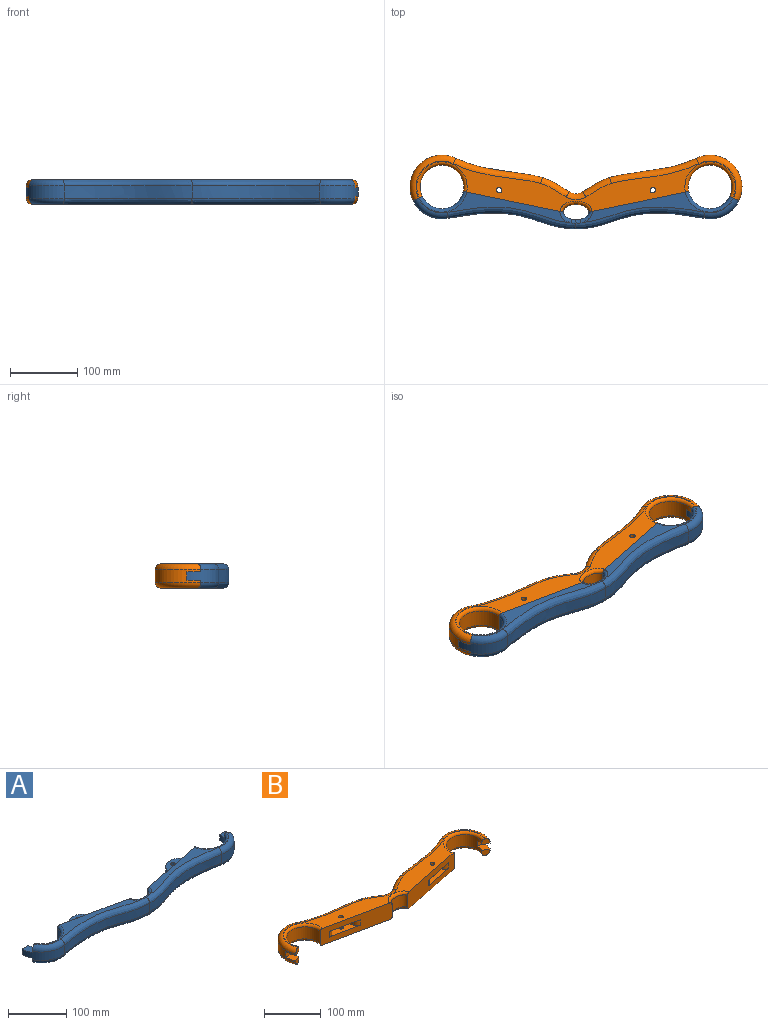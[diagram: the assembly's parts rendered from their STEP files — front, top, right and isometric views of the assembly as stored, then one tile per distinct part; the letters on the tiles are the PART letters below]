
ASSEMBLY  parts=2 mates=1
PART A: 55 faces, bbox 509.2x69.1x37.5 mm
  f0: plane 227x45.55mm, normal (0,0,1), area 2219.1mm2, adj f18,f32,f39,f40,f48,f52
  f1: plane 227x45.55mm, normal (0,0,-1), area 2219.3mm2, adj f20,f27,f33,f34,f45,f46
  f2: cylinder r=47.5mm len=56.8mm, axis (0,0,-1), area 1384.6mm2, adj f3,f17,f25,f26,f31,f32,f36,f40
  f3: plane 15x12mm, normal (0,1,0), area 180mm2, adj f2,f4,f26,f31
  f4: cylinder r=32.5mm len=64.32mm, axis (0,0,-1), area 2279.5mm2, adj f3,f18,f25,f26,f31,f32,f41,f52
  f5: cylinder r=10mm len=12mm, axis (0,0,-1), area 148.4mm2, adj f6,f18,f23,f24
  f6: cylinder r=24.42mm len=45.19mm, axis (0,0,-1), area 725.1mm2, adj f5,f7,f23,f24
  f7: cylinder r=10mm len=12mm, axis (0,0,-1), area 148.4mm2, adj f6,f18,f23,f24
  f8: cylinder r=10mm len=12mm, axis (0,0,-1), area 148.4mm2, adj f9,f20,f21,f22
  f9: cylinder r=24.42mm len=45.19mm, axis (0,0,-1), area 725.1mm2, adj f8,f10,f21,f22
  f10: cylinder r=10mm len=12mm, axis (0,0,-1), area 148.4mm2, adj f9,f20,f21,f22
  f11: cylinder r=32.5mm len=64.32mm, axis (0,0,-1), area 2279.5mm2, adj f12,f20,f27,f28,f29,f30,f46,f47
  f12: plane 15x12mm, normal (0,1,0), area 180mm2, adj f11,f15,f28,f30
  f13: plane 227x45.55mm, normal (0,0,1), area 2219.1mm2, adj f20,f29,f37,f38,f47,f51
  f14: plane 227x45.55mm, normal (0,0,-1), area 2219.1mm2, adj f18,f25,f35,f36,f41,f42
  f15: cylinder r=47.5mm len=56.8mm, axis (0,0,-1), area 1384.6mm2, adj f12,f16,f27,f28,f29,f30,f33,f37
  f16: extruded ~190.33x23.59mm, area 3488.9mm2, adj f15,f17,f34,f38
  f17: extruded ~190.33x23.59mm, area 3488.9mm2, adj f2,f16,f35,f39
  f18: plane 149.04x36.24mm, normal (-0.2,0.98,0), area 4668.3mm2, adj f0,f4,f5,f7,f14,f19,f23,f24
  f19: extruded ~38x26mm, area 1264.1mm2, adj f18,f20,f42,f43,f44,f45,f48,f49
  f20: plane 149.04x36.24mm, normal (0.2,0.98,0), area 4668.3mm2, adj f1,f8,f10,f11,f13,f19,f21,f22
  f21: plane 63.7x29.77mm, normal (0,0,1), area 847.7mm2, adj f8,f9,f10,f20,f54
  f22: plane 63.7x29.77mm, normal (0,0,-1), area 847.7mm2, adj f8,f9,f10,f20,f54
  f23: plane 63.7x29.77mm, normal (0,0,-1), area 847.7mm2, adj f5,f6,f7,f18,f53
  f24: plane 63.7x29.77mm, normal (0,0,1), area 847.7mm2, adj f5,f6,f7,f18,f53
  f25: plane 13.54x12mm, normal (0.43,0.9,0), area 157.3mm2, adj f2,f4,f14,f26,f36,f41
  f26: plane 20.46x18.17mm, normal (0,0,-1), area 267.2mm2, adj f2,f3,f4,f25
  f27: plane 13.54x12mm, normal (-0.43,0.9,0), area 157.3mm2, adj f1,f11,f15,f28,f33,f46
  f28: plane 20.46x18.17mm, normal (0,0,-1), area 267.2mm2, adj f11,f12,f15,f27
  f29: plane 13.54x12mm, normal (-0.43,0.9,0), area 157.3mm2, adj f11,f13,f15,f30,f37,f47
  f30: plane 20.46x18.17mm, normal (0,0,1), area 267.2mm2, adj f11,f12,f15,f29
  f31: plane 20.46x18.17mm, normal (0,0,1), area 267.2mm2, adj f2,f3,f4,f32
  f32: plane 13.54x12mm, normal (0.43,0.9,0), area 157.3mm2, adj f0,f2,f4,f31,f40,f52
  f33: torus R=38.5mm, axis (0,0,1), area 826.9mm2, adj f1,f15,f27,f34
  f34: bspline ~289x32.96mm, area 2745mm2, adj f1,f16,f33,f35,f44
  f35: bspline ~289x32.96mm, area 2745mm2, adj f14,f17,f34,f36,f43
  f36: torus R=38.5mm, axis (0,0,1), area 826.9mm2, adj f2,f14,f25,f35
  f37: torus R=38.5mm, axis (0,0,1), area 826.9mm2, adj f13,f15,f29,f38
  f38: bspline ~289x32.96mm, area 2745mm2, adj f13,f16,f37,f39,f50
  f39: bspline ~289x32.96mm, area 2745mm2, adj f0,f17,f38,f40,f49
  f40: torus R=38.5mm, axis (0,0,1), area 826.9mm2, adj f0,f2,f32,f39
  f41: torus R=37.5mm, axis (0,0,1), area 671.7mm2, adj f4,f14,f18,f25
  f42: bspline ~18.81x18.43mm, area 163.5mm2, adj f14,f18,f19,f43
  f43: bspline ~9.26x6.45mm, area 56.4mm2, adj f19,f35,f42,f44
  f44: bspline ~9.26x6.45mm, area 56.4mm2, adj f19,f34,f43,f45
  f45: bspline ~20.39x19.55mm, area 163.5mm2, adj f1,f19,f20,f44
  f46: torus R=37.5mm, axis (0,0,1), area 671.7mm2, adj f1,f11,f20,f27
  f47: torus R=37.5mm, axis (0,0,1), area 671.7mm2, adj f11,f13,f20,f29
  f48: bspline ~20.39x19.55mm, area 163.5mm2, adj f0,f18,f19,f49
  f49: bspline ~9.26x6.45mm, area 56.4mm2, adj f19,f39,f48,f50
  f50: bspline ~9.26x6.45mm, area 56.4mm2, adj f19,f38,f49,f51
  f51: bspline ~18.8x18.43mm, area 163.5mm2, adj f13,f19,f20,f50
  f52: torus R=37.5mm, axis (0,0,1), area 671.7mm2, adj f0,f4,f18,f32
  f53: cylinder r=4mm len=12mm, axis (0,0,1), area 301.6mm2, adj f23,f24
  f54: cylinder r=4mm len=12mm, axis (0,0,1), area 301.6mm2, adj f21,f22
PART B: 58 faces, bbox 502.3x93.3x36.2 mm
  f0: plane 476.25x74.89mm, normal (0,0,1), area 10070.9mm2, adj f14,f16,f25,f26,f41,f42,f43,f44
  f1: plane 476.25x74.89mm, normal (0,0,-1), area 10070.9mm2, adj f14,f16,f31,f32,f34,f35,f36,f37
  f2: cylinder r=47.5mm len=68.15mm, axis (0,0,-1), area 1854.6mm2, adj f3,f21,f24,f25,f28,f32,f34,f47
  f3: extruded ~128.97x28.78mm, area 2388.7mm2, adj f2,f4,f35,f46
  f4: extruded ~40x21.26mm, area 817.9mm2, adj f3,f5,f36,f45
  f5: cylinder r=20mm len=19.99mm, axis (0,0,-1), area 376.8mm2, adj f4,f6,f37,f44
  f6: extruded ~40x21.26mm, area 817.9mm2, adj f5,f7,f38,f43
  f7: extruded ~128.97x28.78mm, area 2388.7mm2, adj f6,f8,f39,f42
  f8: cylinder r=47.5mm len=68.15mm, axis (0,0,-1), area 1854.6mm2, adj f7,f9,f22,f26,f30,f31,f40,f41
  f9: plane 15x12mm, normal (0,-1,0), area 180mm2, adj f8,f10,f22,f30
  f10: cylinder r=32.5mm len=65mm, axis (0,0,-1), area 3029.8mm2, adj f9,f14,f22,f26,f30,f31,f50,f52
  f11: cylinder r=10mm len=12mm, axis (0,0,-1), area 148.4mm2, adj f12,f14,f27,f29
  f12: cylinder r=24.42mm len=45.19mm, axis (0,0,-1), area 725.1mm2, adj f11,f13,f27,f29
  f13: cylinder r=10mm len=12mm, axis (0,0,-1), area 148.4mm2, adj f12,f14,f27,f29
  f14: plane 149.04x36.24mm, normal (-0.2,-0.98,0), area 4668.3mm2, adj f0,f1,f10,f11,f13,f15,f27,f29
  f15: extruded ~38x26mm, area 1264.5mm2, adj f14,f16,f48,f53
  f16: plane 149.04x36.24mm, normal (0.2,-0.98,0), area 4668.3mm2, adj f0,f1,f15,f17,f19,f20,f23,f33
  f17: cylinder r=10mm len=12mm, axis (0,0,-1), area 148.4mm2, adj f16,f18,f23,f33
  f18: cylinder r=24.42mm len=45.19mm, axis (0,0,-1), area 725.1mm2, adj f17,f19,f23,f33
  f19: cylinder r=10mm len=12mm, axis (0,0,-1), area 148.4mm2, adj f16,f18,f23,f33
  f20: cylinder r=32.5mm len=65mm, axis (0,0,-1), area 3029.8mm2, adj f16,f21,f24,f25,f28,f32,f49,f51
  f21: plane 15x12mm, normal (0,-1,0), area 180mm2, adj f2,f20,f24,f28
  f22: plane 20.46x18.17mm, normal (0,0,-1), area 267.2mm2, adj f8,f9,f10,f26
  f23: plane 63.7x29.77mm, normal (0,0,-1), area 847.7mm2, adj f16,f17,f18,f19,f57
  f24: plane 20.46x18.17mm, normal (0,0,-1), area 267.2mm2, adj f2,f20,f21,f25
  f25: plane 13.54x12mm, normal (-0.43,-0.9,0), area 157.3mm2, adj f0,f2,f20,f24,f47,f51
  f26: plane 13.54x12mm, normal (0.43,-0.9,0), area 157.3mm2, adj f0,f8,f10,f22,f41,f52
  f27: plane 63.7x29.77mm, normal (0,0,-1), area 847.7mm2, adj f11,f12,f13,f14,f56
  f28: plane 20.46x18.17mm, normal (0,0,1), area 267.2mm2, adj f2,f20,f21,f32
  f29: plane 63.7x29.77mm, normal (0,0,1), area 847.7mm2, adj f11,f12,f13,f14,f55
  f30: plane 20.46x18.17mm, normal (0,0,1), area 267.2mm2, adj f8,f9,f10,f31
  f31: plane 13.54x12mm, normal (0.43,-0.9,0), area 157.3mm2, adj f1,f8,f10,f30,f40,f50
  f32: plane 13.54x12mm, normal (-0.43,-0.9,0), area 157.3mm2, adj f1,f2,f20,f28,f34,f49
  f33: plane 63.7x29.77mm, normal (0,0,1), area 847.7mm2, adj f16,f17,f18,f19,f54
  f34: torus R=38.5mm, axis (0,0,-1), area 1541.9mm2, adj f1,f2,f32,f35
  f35: bspline ~182.32x56.96mm, area 1882.8mm2, adj f1,f3,f34,f36
  f36: bspline ~59.06x36.24mm, area 632.3mm2, adj f1,f4,f35,f37
  f37: torus R=29mm, axis (0,0,-1), area 344.4mm2, adj f1,f5,f36,f38
  f38: bspline ~53.17x32.87mm, area 632.3mm2, adj f1,f6,f37,f39
  f39: bspline ~163.62x50.96mm, area 1882.8mm2, adj f1,f7,f38,f40
  f40: torus R=38.5mm, axis (0,0,-1), area 1541.9mm2, adj f1,f8,f31,f39
  f41: torus R=38.5mm, axis (0,0,1), area 1541.9mm2, adj f0,f8,f26,f42
  f42: bspline ~182.32x56.96mm, area 1882.8mm2, adj f0,f7,f41,f43
  f43: bspline ~59.06x36.24mm, area 632.3mm2, adj f0,f6,f42,f44
  f44: torus R=29mm, axis (0,0,1), area 344.4mm2, adj f0,f5,f43,f45
  f45: bspline ~59.06x36.24mm, area 632.3mm2, adj f0,f4,f44,f46
  f46: bspline ~182.32x56.96mm, area 1882.8mm2, adj f0,f3,f45,f47
  f47: torus R=38.5mm, axis (0,0,1), area 1541.9mm2, adj f0,f2,f25,f46
  f48: bspline ~48.01x17.77mm, area 420.3mm2, adj f1,f14,f15,f16
  f49: torus R=37.5mm, axis (0,0,-1), area 1021.8mm2, adj f1,f16,f20,f32
  f50: torus R=37.5mm, axis (0,0,-1), area 1021.8mm2, adj f1,f10,f14,f31
  f51: torus R=37.5mm, axis (0,0,1), area 1021.8mm2, adj f0,f16,f20,f25
  f52: torus R=37.5mm, axis (0,0,1), area 1021.8mm2, adj f0,f10,f14,f26
  f53: bspline ~48.01x17.77mm, area 420.3mm2, adj f0,f14,f15,f16
  f54: cylinder r=4mm len=12mm, axis (0,0,1), area 301.6mm2, adj f1,f33
  f55: cylinder r=4mm len=12mm, axis (0,0,1), area 301.6mm2, adj f1,f29
  f56: cylinder r=4mm len=12mm, axis (0,0,1), area 301.6mm2, adj f0,f27
  f57: cylinder r=4mm len=12mm, axis (0,0,1), area 301.6mm2, adj f0,f23
PLACE A at identity fixed
PLACE B at identity
MATE fastened B.f21 <-> A.f3  axis (0,-1,0) through (239.63,37.41,0)mm
